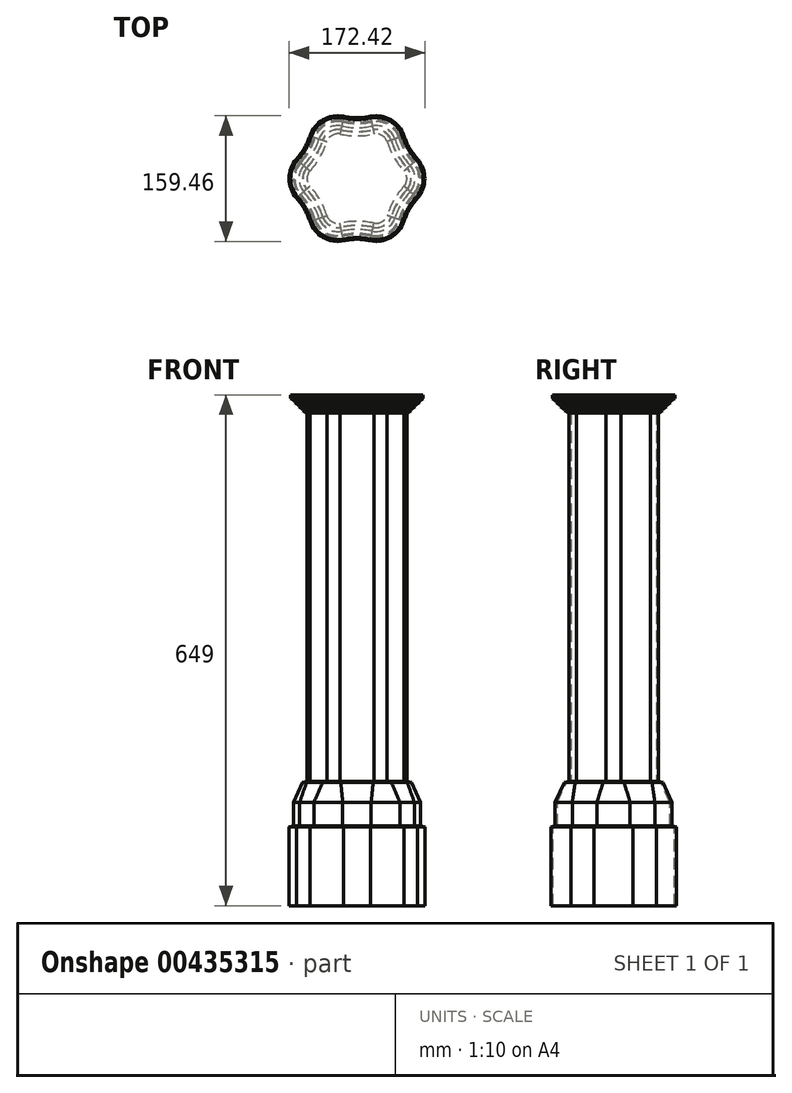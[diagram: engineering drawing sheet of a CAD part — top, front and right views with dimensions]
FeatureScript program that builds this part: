
annotation { "Feature Type Name" : "Feature", "Feature Type Description" : "" }
export const myFeature = defineFeature(function(context is Context, id is Id, definition is map)
    precondition{}
    {
        {
            var Q0;
            Q0=qCreatedBy(makeId("Top.planeOp"),FACE);
            var sketch = newSketch(context, id + "F0", { "sketchPlane" : qUnion([Q0])});
            skCircle(sketch, "E0.cCircle", {"center": v(0, 0) * mm, "radius": 60.62 * mm, "construction": true});
            skLineSegment(sketch, "E0.0", {"start": v(35, -60.62) * mm, "end": v(-35, -60.62) * mm});
            skLineSegment(sketch, "E0.1", {"start": v(-35, -60.62) * mm, "end": v(-70, 0) * mm});
            skLineSegment(sketch, "E0.2", {"start": v(-70, 0) * mm, "end": v(-35, 60.62) * mm});
            skLineSegment(sketch, "E0.3", {"start": v(-35, 60.62) * mm, "end": v(35, 60.62) * mm});
            skLineSegment(sketch, "E0.4", {"start": v(35, 60.62) * mm, "end": v(70, 0) * mm});
            skLineSegment(sketch, "E0.5", {"start": v(70, 0) * mm, "end": v(35, -60.62) * mm});
            skPoint(sketch, "E0.0.midPoint", {"position": v(0, -60.62) * mm});
            skArc(sketch, "E1", {"start": v(-70, 0) * mm, "mid": v(-47.02, 27.15) * mm, "end": v(-35, 60.62) * mm});
            skArc(sketch, "E2", {"start": v(-35, 60.62) * mm, "mid": v(0, 54.3) * mm, "end": v(35, 60.62) * mm});
            skArc(sketch, "E3.1.0", {"start": v(35, -60.62) * mm, "mid": v(0, -54.3) * mm, "end": v(-35, -60.62) * mm});
            skArc(sketch, "E3.1.1", {"start": v(-35, -60.62) * mm, "mid": v(-47.02, -27.15) * mm, "end": v(-70, 0) * mm});
            skArc(sketch, "E3.2.0", {"start": v(35, 60.62) * mm, "mid": v(47.02, 27.15) * mm, "end": v(70, 0) * mm});
            skArc(sketch, "E3.2.1", {"start": v(70, 0) * mm, "mid": v(47.02, -27.15) * mm, "end": v(35, -60.62) * mm});
            skArc(sketch, "E4", {"start": v(-21.58, 56.65) * mm, "mid": v(-31.68, 54.87) * mm, "end": v(-38.27, 47.01) * mm});
            skArc(sketch, "E5.1.0", {"start": v(-59.85, 9.64) * mm, "mid": v(-63.36, 0) * mm, "end": v(-59.85, -9.64) * mm});
            skArc(sketch, "E5.2.0", {"start": v(-38.27, -47.01) * mm, "mid": v(-31.68, -54.87) * mm, "end": v(-21.58, -56.65) * mm});
            skArc(sketch, "E5.3.0", {"start": v(21.58, -56.65) * mm, "mid": v(31.68, -54.87) * mm, "end": v(38.27, -47.01) * mm});
            skArc(sketch, "E5.4.0", {"start": v(59.85, -9.64) * mm, "mid": v(63.36, 0) * mm, "end": v(59.85, 9.64) * mm});
            skArc(sketch, "E5.5.0", {"start": v(38.27, 47.01) * mm, "mid": v(31.68, 54.87) * mm, "end": v(21.58, 56.65) * mm});
            skSolve(sketch);
        }
        {
            var Q0;
            {var subQ7=sQuery(id+"F0.wireOp",EDGE,"E4");Q0=makeQuery(id+"F0.imprint","IMPRINT",FACE,{"disambiguationData":[TD([[makeQuery(id+"F0.imprint","IMPRINT",EDGE,{"derivedFrom":subQ7}),1.0]])]});}
            extrude(context, id + "F1", {"entities" : qUnion([Q0]), "depth" : 468 * mm});
        }
        {
            var Q0;
            Q0=makeQuery(id+"F1.opExtrude","CAP_FACE",FACE,{"disambiguationData":[OSD([sQuery(id+"F0.wireOp",EDGE,"E1"),sQuery(id+"F0.wireOp",EDGE,"E2"),sQuery(id+"F0.wireOp",EDGE,"E3.1.0"),sQuery(id+"F0.wireOp",EDGE,"E3.1.1"),sQuery(id+"F0.wireOp",EDGE,"E3.2.0"),sQuery(id+"F0.wireOp",EDGE,"E3.2.1"),sQuery(id+"F0.wireOp",EDGE,"E4"),sQuery(id+"F0.wireOp",EDGE,"E5.1.0"),sQuery(id+"F0.wireOp",EDGE,"E5.2.0"),sQuery(id+"F0.wireOp",EDGE,"E5.3.0"),sQuery(id+"F0.wireOp",EDGE,"E5.4.0"),sQuery(id+"F0.wireOp",EDGE,"E5.5.0")])],"isStart":false});
            extrude(context, id + "F2", {"entities" : qUnion([Q0]), "operationType" : NewBodyOperationType.ADD, "depth" : 3 * mm, "hasDraft" : true, "draftAngle" : 60 * degree});
        }
        {
            var Q0;
            Q0=makeQuery(id+"F2.opExtrude","CAP_FACE",FACE,{"disambiguationData":[OSD([sQuery(id+"F0.wireOp",EDGE,"E1"),sQuery(id+"F0.wireOp",EDGE,"E2"),sQuery(id+"F0.wireOp",EDGE,"E3.1.0"),sQuery(id+"F0.wireOp",EDGE,"E3.1.1"),sQuery(id+"F0.wireOp",EDGE,"E3.2.0"),sQuery(id+"F0.wireOp",EDGE,"E3.2.1"),sQuery(id+"F0.wireOp",EDGE,"E4"),sQuery(id+"F0.wireOp",EDGE,"E5.1.0"),sQuery(id+"F0.wireOp",EDGE,"E5.2.0"),sQuery(id+"F0.wireOp",EDGE,"E5.3.0"),sQuery(id+"F0.wireOp",EDGE,"E5.4.0"),sQuery(id+"F0.wireOp",EDGE,"E5.5.0")])],"isStart":false});
            extrude(context, id + "F3", {"entities" : qUnion([Q0]), "operationType" : NewBodyOperationType.ADD, "depth" : 2 * mm});
        }
        {
            var Q0;
            Q0=makeQuery(id+"F3.opExtrude","CAP_FACE",FACE,{"disambiguationData":[OSD([sQuery(id+"F0.wireOp",EDGE,"E1"),sQuery(id+"F0.wireOp",EDGE,"E2"),sQuery(id+"F0.wireOp",EDGE,"E3.1.0"),sQuery(id+"F0.wireOp",EDGE,"E3.1.1"),sQuery(id+"F0.wireOp",EDGE,"E3.2.0"),sQuery(id+"F0.wireOp",EDGE,"E3.2.1"),sQuery(id+"F0.wireOp",EDGE,"E4"),sQuery(id+"F0.wireOp",EDGE,"E5.1.0"),sQuery(id+"F0.wireOp",EDGE,"E5.2.0"),sQuery(id+"F0.wireOp",EDGE,"E5.3.0"),sQuery(id+"F0.wireOp",EDGE,"E5.4.0"),sQuery(id+"F0.wireOp",EDGE,"E5.5.0")])],"isStart":false});
            extrude(context, id + "F4", {"entities" : qUnion([Q0]), "operationType" : NewBodyOperationType.ADD, "depth" : 3 * mm, "hasDraft" : true, "draftAngle" : 60 * degree});
        }
        {
            var Q0;
            Q0=makeQuery(id+"F4.opExtrude","CAP_FACE",FACE,{"disambiguationData":[OSD([sQuery(id+"F0.wireOp",EDGE,"E1"),sQuery(id+"F0.wireOp",EDGE,"E2"),sQuery(id+"F0.wireOp",EDGE,"E3.1.0"),sQuery(id+"F0.wireOp",EDGE,"E3.1.1"),sQuery(id+"F0.wireOp",EDGE,"E3.2.0"),sQuery(id+"F0.wireOp",EDGE,"E3.2.1"),sQuery(id+"F0.wireOp",EDGE,"E4"),sQuery(id+"F0.wireOp",EDGE,"E5.1.0"),sQuery(id+"F0.wireOp",EDGE,"E5.2.0"),sQuery(id+"F0.wireOp",EDGE,"E5.3.0"),sQuery(id+"F0.wireOp",EDGE,"E5.4.0"),sQuery(id+"F0.wireOp",EDGE,"E5.5.0")])],"isStart":false});
            extrude(context, id + "F5", {"entities" : qUnion([Q0]), "operationType" : NewBodyOperationType.ADD, "depth" : 2 * mm});
        }
        {
            var Q0;
            Q0=makeQuery(id+"F5.opExtrude","CAP_FACE",FACE,{"disambiguationData":[OSD([sQuery(id+"F0.wireOp",EDGE,"E1"),sQuery(id+"F0.wireOp",EDGE,"E2"),sQuery(id+"F0.wireOp",EDGE,"E3.1.0"),sQuery(id+"F0.wireOp",EDGE,"E3.1.1"),sQuery(id+"F0.wireOp",EDGE,"E3.2.0"),sQuery(id+"F0.wireOp",EDGE,"E3.2.1"),sQuery(id+"F0.wireOp",EDGE,"E4"),sQuery(id+"F0.wireOp",EDGE,"E5.1.0"),sQuery(id+"F0.wireOp",EDGE,"E5.2.0"),sQuery(id+"F0.wireOp",EDGE,"E5.3.0"),sQuery(id+"F0.wireOp",EDGE,"E5.4.0"),sQuery(id+"F0.wireOp",EDGE,"E5.5.0")])],"isStart":false});
            extrude(context, id + "F6", {"entities" : qUnion([Q0]), "operationType" : NewBodyOperationType.ADD, "depth" : 3 * mm, "hasDraft" : true, "draftAngle" : 60 * degree});
        }
        {
            var Q0;
            Q0=makeQuery(id+"F6.opExtrude","CAP_FACE",FACE,{"disambiguationData":[OSD([sQuery(id+"F0.wireOp",EDGE,"E1"),sQuery(id+"F0.wireOp",EDGE,"E2"),sQuery(id+"F0.wireOp",EDGE,"E3.1.0"),sQuery(id+"F0.wireOp",EDGE,"E3.1.1"),sQuery(id+"F0.wireOp",EDGE,"E3.2.0"),sQuery(id+"F0.wireOp",EDGE,"E3.2.1"),sQuery(id+"F0.wireOp",EDGE,"E4"),sQuery(id+"F0.wireOp",EDGE,"E5.1.0"),sQuery(id+"F0.wireOp",EDGE,"E5.2.0"),sQuery(id+"F0.wireOp",EDGE,"E5.3.0"),sQuery(id+"F0.wireOp",EDGE,"E5.4.0"),sQuery(id+"F0.wireOp",EDGE,"E5.5.0")])],"isStart":false});
            extrude(context, id + "F7", {"entities" : qUnion([Q0]), "operationType" : NewBodyOperationType.ADD, "depth" : 2 * mm});
        }
        {
            var Q0;
            Q0=makeQuery(id+"F7.opExtrude","CAP_FACE",FACE,{"disambiguationData":[OSD([sQuery(id+"F0.wireOp",EDGE,"E1"),sQuery(id+"F0.wireOp",EDGE,"E2"),sQuery(id+"F0.wireOp",EDGE,"E3.1.0"),sQuery(id+"F0.wireOp",EDGE,"E3.1.1"),sQuery(id+"F0.wireOp",EDGE,"E3.2.0"),sQuery(id+"F0.wireOp",EDGE,"E3.2.1"),sQuery(id+"F0.wireOp",EDGE,"E4"),sQuery(id+"F0.wireOp",EDGE,"E5.1.0"),sQuery(id+"F0.wireOp",EDGE,"E5.2.0"),sQuery(id+"F0.wireOp",EDGE,"E5.3.0"),sQuery(id+"F0.wireOp",EDGE,"E5.4.0"),sQuery(id+"F0.wireOp",EDGE,"E5.5.0")])],"isStart":false});
            extrude(context, id + "F8", {"entities" : qUnion([Q0]), "operationType" : NewBodyOperationType.ADD, "depth" : 3 * mm, "hasDraft" : true, "draftAngle" : 60 * degree});
        }
        {
            var Q0;
            Q0=makeQuery(id+"F8.opExtrude","CAP_FACE",FACE,{"disambiguationData":[OSD([sQuery(id+"F0.wireOp",EDGE,"E1"),sQuery(id+"F0.wireOp",EDGE,"E2"),sQuery(id+"F0.wireOp",EDGE,"E3.1.0"),sQuery(id+"F0.wireOp",EDGE,"E3.1.1"),sQuery(id+"F0.wireOp",EDGE,"E3.2.0"),sQuery(id+"F0.wireOp",EDGE,"E3.2.1"),sQuery(id+"F0.wireOp",EDGE,"E4"),sQuery(id+"F0.wireOp",EDGE,"E5.1.0"),sQuery(id+"F0.wireOp",EDGE,"E5.2.0"),sQuery(id+"F0.wireOp",EDGE,"E5.3.0"),sQuery(id+"F0.wireOp",EDGE,"E5.4.0"),sQuery(id+"F0.wireOp",EDGE,"E5.5.0")])],"isStart":false});
            extrude(context, id + "F9", {"entities" : qUnion([Q0]), "operationType" : NewBodyOperationType.ADD, "depth" : 5 * mm});
        }
        {
            var Q0;
            Q0=makeQuery(id+"F1.opExtrude","CAP_FACE",FACE,{"disambiguationData":[OSD([sQuery(id+"F0.wireOp",EDGE,"E1"),sQuery(id+"F0.wireOp",EDGE,"E2"),sQuery(id+"F0.wireOp",EDGE,"E3.1.0"),sQuery(id+"F0.wireOp",EDGE,"E3.1.1"),sQuery(id+"F0.wireOp",EDGE,"E3.2.0"),sQuery(id+"F0.wireOp",EDGE,"E3.2.1"),sQuery(id+"F0.wireOp",EDGE,"E4"),sQuery(id+"F0.wireOp",EDGE,"E5.1.0"),sQuery(id+"F0.wireOp",EDGE,"E5.2.0"),sQuery(id+"F0.wireOp",EDGE,"E5.3.0"),sQuery(id+"F0.wireOp",EDGE,"E5.4.0"),sQuery(id+"F0.wireOp",EDGE,"E5.5.0")])],"isStart":true});
            extrude(context, id + "F10", {"entities" : qUnion([Q0]), "depth" : 1.5 * mm, "hasDraft" : true, "draftAngle" : 75 * degree});
        }
        {
            var Q0;
            Q0=makeQuery(id+"F10.opExtrude","CAP_FACE",FACE,{"disambiguationData":[OSD([sQuery(id+"F0.wireOp",EDGE,"E1"),sQuery(id+"F0.wireOp",EDGE,"E2"),sQuery(id+"F0.wireOp",EDGE,"E3.1.0"),sQuery(id+"F0.wireOp",EDGE,"E3.1.1"),sQuery(id+"F0.wireOp",EDGE,"E3.2.0"),sQuery(id+"F0.wireOp",EDGE,"E3.2.1"),sQuery(id+"F0.wireOp",EDGE,"E4"),sQuery(id+"F0.wireOp",EDGE,"E5.1.0"),sQuery(id+"F0.wireOp",EDGE,"E5.2.0"),sQuery(id+"F0.wireOp",EDGE,"E5.3.0"),sQuery(id+"F0.wireOp",EDGE,"E5.4.0"),sQuery(id+"F0.wireOp",EDGE,"E5.5.0")])],"isStart":false});
            extrude(context, id + "F11", {"entities" : qUnion([Q0]), "operationType" : NewBodyOperationType.ADD, "depth" : 25 * mm, "hasDraft" : true, "draftAngle" : 25 * degree});
        }
        {
            var Q0;
            Q0=makeQuery(id+"F11.opExtrude","CAP_FACE",FACE,{"disambiguationData":[OSD([sQuery(id+"F0.wireOp",EDGE,"E1"),sQuery(id+"F0.wireOp",EDGE,"E2"),sQuery(id+"F0.wireOp",EDGE,"E3.1.0"),sQuery(id+"F0.wireOp",EDGE,"E3.1.1"),sQuery(id+"F0.wireOp",EDGE,"E3.2.0"),sQuery(id+"F0.wireOp",EDGE,"E3.2.1"),sQuery(id+"F0.wireOp",EDGE,"E4"),sQuery(id+"F0.wireOp",EDGE,"E5.1.0"),sQuery(id+"F0.wireOp",EDGE,"E5.2.0"),sQuery(id+"F0.wireOp",EDGE,"E5.3.0"),sQuery(id+"F0.wireOp",EDGE,"E5.4.0"),sQuery(id+"F0.wireOp",EDGE,"E5.5.0")])],"isStart":false});
            extrude(context, id + "F12", {"entities" : qUnion([Q0]), "operationType" : NewBodyOperationType.ADD, "depth" : 30 * mm});
        }
        {
            var Q0;
            Q0=makeQuery(id+"F12.opExtrude","CAP_FACE",FACE,{"disambiguationData":[OSD([sQuery(id+"F0.wireOp",EDGE,"E1"),sQuery(id+"F0.wireOp",EDGE,"E2"),sQuery(id+"F0.wireOp",EDGE,"E3.1.0"),sQuery(id+"F0.wireOp",EDGE,"E3.1.1"),sQuery(id+"F0.wireOp",EDGE,"E3.2.0"),sQuery(id+"F0.wireOp",EDGE,"E3.2.1"),sQuery(id+"F0.wireOp",EDGE,"E4"),sQuery(id+"F0.wireOp",EDGE,"E5.1.0"),sQuery(id+"F0.wireOp",EDGE,"E5.2.0"),sQuery(id+"F0.wireOp",EDGE,"E5.3.0"),sQuery(id+"F0.wireOp",EDGE,"E5.4.0"),sQuery(id+"F0.wireOp",EDGE,"E5.5.0")])],"isStart":false});
            extrude(context, id + "F13", {"entities" : qUnion([Q0]), "operationType" : NewBodyOperationType.ADD, "depth" : 1.5 * mm, "hasDraft" : true, "draftAngle" : 75 * degree});
        }
        {
            var Q0;
            Q0=makeQuery(id+"F13.opExtrude","CAP_FACE",FACE,{"disambiguationData":[OSD([sQuery(id+"F0.wireOp",EDGE,"E1"),sQuery(id+"F0.wireOp",EDGE,"E2"),sQuery(id+"F0.wireOp",EDGE,"E3.1.0"),sQuery(id+"F0.wireOp",EDGE,"E3.1.1"),sQuery(id+"F0.wireOp",EDGE,"E3.2.0"),sQuery(id+"F0.wireOp",EDGE,"E3.2.1"),sQuery(id+"F0.wireOp",EDGE,"E4"),sQuery(id+"F0.wireOp",EDGE,"E5.1.0"),sQuery(id+"F0.wireOp",EDGE,"E5.2.0"),sQuery(id+"F0.wireOp",EDGE,"E5.3.0"),sQuery(id+"F0.wireOp",EDGE,"E5.4.0"),sQuery(id+"F0.wireOp",EDGE,"E5.5.0")])],"isStart":false});
            extrude(context, id + "F14", {"entities" : qUnion([Q0]), "operationType" : NewBodyOperationType.ADD, "depth" : 100 * mm});
        }
    });
